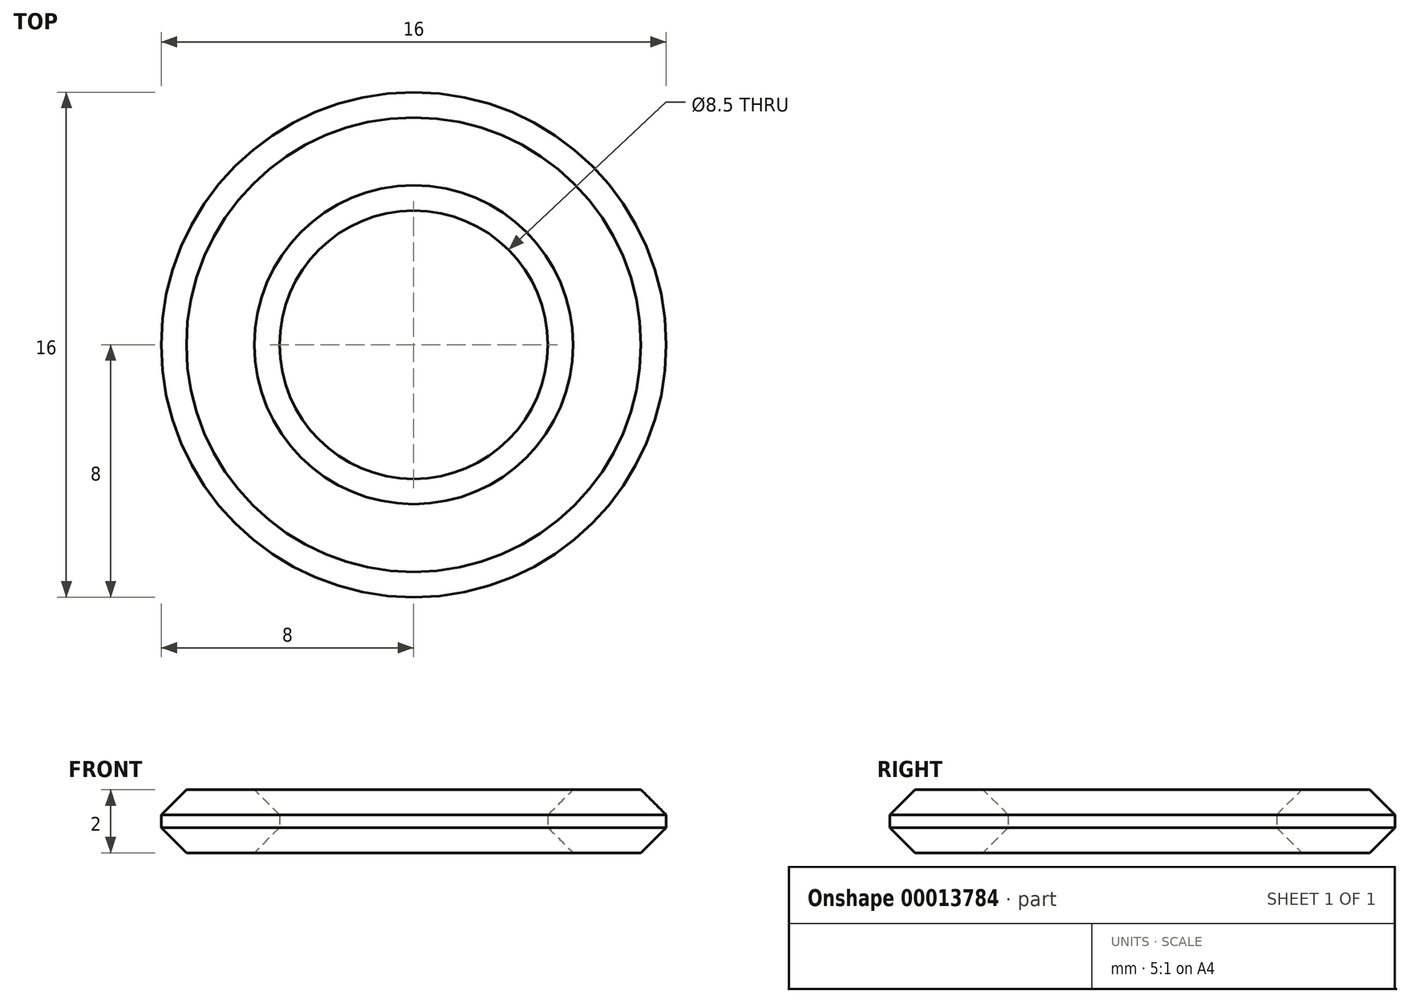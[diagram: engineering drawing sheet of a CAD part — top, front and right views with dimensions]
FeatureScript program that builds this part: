
annotation { "Feature Type Name" : "Feature", "Feature Type Description" : "" }
export const myFeature = defineFeature(function(context is Context, id is Id, definition is map)
    precondition{}
    {
        {
            var Q0;
            Q0=qCreatedBy(makeId("Top.planeOp"),FACE);
            var sketch = newSketch(context, id + "F0", { "sketchPlane" : qUnion([Q0])});
            skCircle(sketch, "E0", {"center": v(0, 0) * mm, "radius": 8 * mm});
            skCircle(sketch, "E1", {"center": v(0, 0) * mm, "radius": 4.25 * mm});
            skSolve(sketch);
        }
        {
            var Q0;
            Q0=makeQuery(id+"F0.imprint","IMPRINT",FACE,{"disambiguationData":[TD([[makeQuery(id+"F0.imprint","IMPRINT",EDGE,{"derivedFrom":sQuery(id+"F0.wireOp",EDGE,"E0")}),1.0]])]});
            extrude(context, id + "F1", {"entities" : qUnion([Q0]), "depth" : 2 * mm});
        }
        {
            var Q0;
            Q0=makeQuery(id+"F1.opExtrude","CAP_EDGE",EDGE,{"disambiguationData":[OSD([sQuery(id+"F0.wireOp",EDGE,"E0")])],"isStart":false});
            var Q1;
            Q1=makeQuery(id+"F1.opExtrude","CAP_EDGE",EDGE,{"disambiguationData":[OSD([sQuery(id+"F0.wireOp",EDGE,"E1")])],"isStart":false});
            var Q2;
            Q2=makeQuery(id+"F1.opExtrude","CAP_EDGE",EDGE,{"disambiguationData":[OSD([sQuery(id+"F0.wireOp",EDGE,"E0")])],"isStart":true});
            var Q3;
            Q3=makeQuery(id+"F1.opExtrude","CAP_EDGE",EDGE,{"disambiguationData":[OSD([sQuery(id+"F0.wireOp",EDGE,"E1")])],"isStart":true});
            chamfer(context, id + "F2", {"entities" : qUnion([Q0, Q1, Q2, Q3]), "width" : 0.8 * mm, "tangentPropagation" : true});
        }
    });
